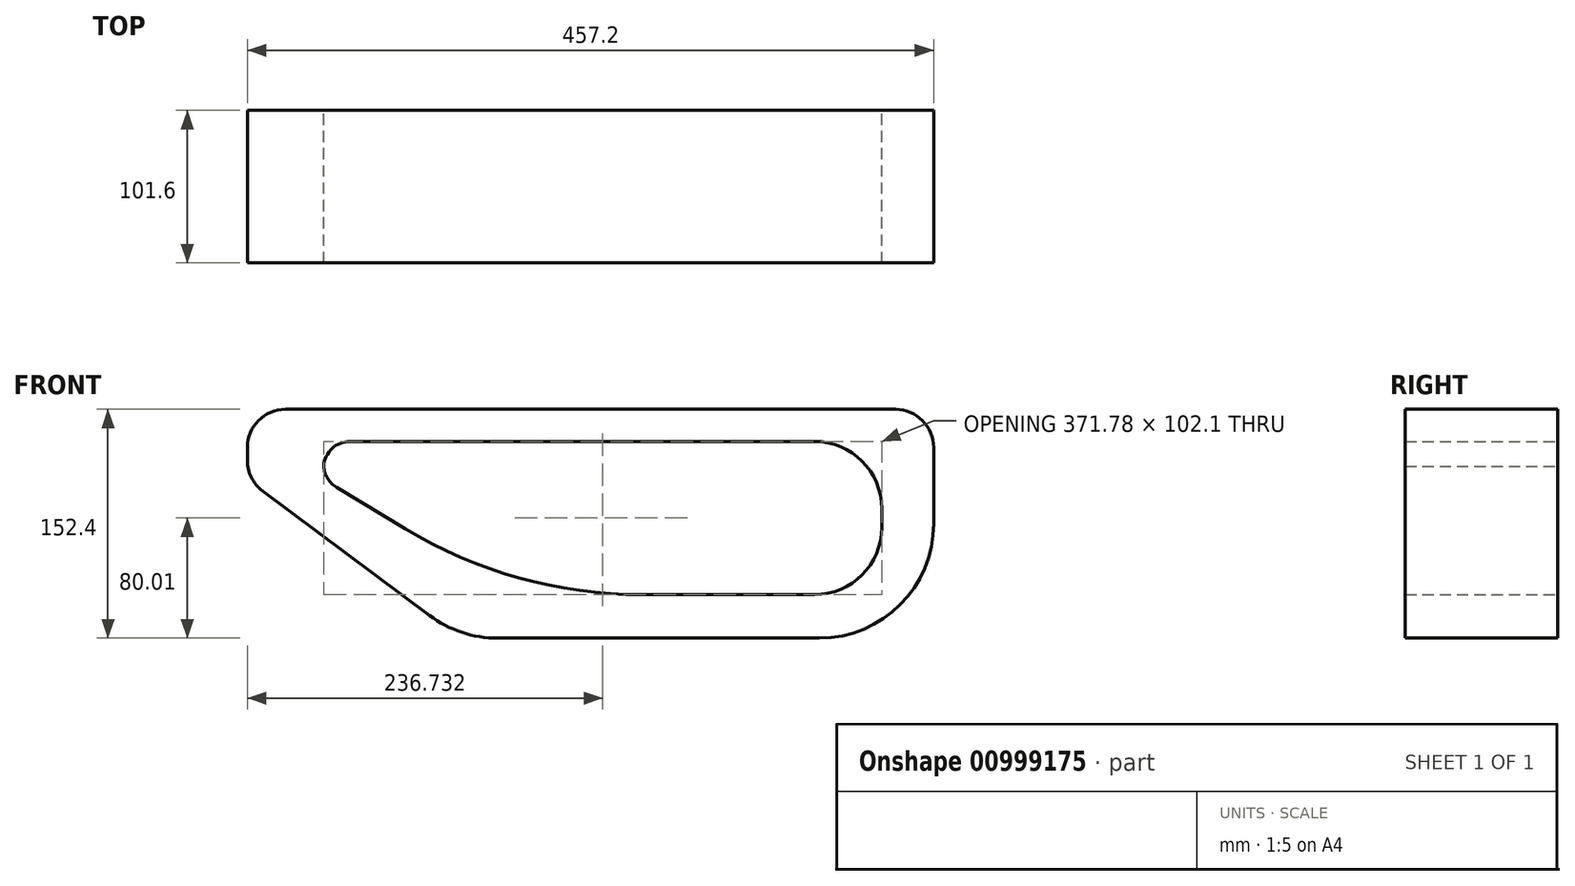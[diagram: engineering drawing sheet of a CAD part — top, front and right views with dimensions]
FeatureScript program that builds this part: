
annotation { "Feature Type Name" : "Feature", "Feature Type Description" : "" }
export const myFeature = defineFeature(function(context is Context, id is Id, definition is map)
    precondition{}
    {
        {
            var Q0;
            Q0=qCreatedBy(makeId("Front.planeOp"),FACE);
            var sketch = newSketch(context, id + "F0", { "sketchPlane" : qUnion([Q0])});
            skLineSegment(sketch, "E0.top", {"start": v(228.6, 76.2) * mm, "end": v(-228.6, 76.2) * mm});
            skLineSegment(sketch, "E0.left", {"start": v(228.6, -76.2) * mm, "end": v(228.6, 76.2) * mm});
            skPoint(sketch, "E0.middle", {"position": v(0, 0) * mm});
            skLineSegment(sketch, "E1", {"start": v(-228.6, 29.46) * mm, "end": v(-86.97, -76.2) * mm});
            skLineSegment(sketch, "E2", {"start": v(-177.8, 29.46) * mm, "end": v(-50.81, -47.24) * mm});
            skLineSegment(sketch, "E3", {"start": v(-50.81, -47.24) * mm, "end": v(194.02, -47.24) * mm});
            skLineSegment(sketch, "E4", {"start": v(-86.97, -76.2) * mm, "end": v(228.6, -76.2) * mm});
            skLineSegment(sketch, "E5", {"start": v(-228.6, 76.2) * mm, "end": v(-228.6, 29.46) * mm});
            skLineSegment(sketch, "E6", {"start": v(-177.8, 29.46) * mm, "end": v(-177.8, 54.86) * mm});
            skLineSegment(sketch, "E7", {"start": v(-177.8, 54.86) * mm, "end": v(194.02, 54.86) * mm});
            skLineSegment(sketch, "E8", {"start": v(194.02, 54.86) * mm, "end": v(194.02, -47.24) * mm});
            skSolve(sketch);
        }
        {
            var Q0;
            Q0=makeQuery(id+"F0.imprint","IMPRINT",FACE,{"disambiguationData":[TD([[makeQuery(id+"F0.imprint","IMPRINT",EDGE,{"derivedFrom":sQuery(id+"F0.wireOp",EDGE,"E0.top")}),1.0]])]});
            extrude(context, id + "F1", {"entities" : qUnion([Q0]), "depth" : 101.6 * mm, "offsetDistance" : 25.4 * mm});
        }
        {
            var Q0;
            Q0=makeQuery(id+"F1.opExtrude","SWEPT_EDGE",EDGE,{"disambiguationData":[OSD([sQuery(id+"F0.wireOp",EDGE,"E0.top"),sQuery(id+"F0.wireOp",EDGE,"E5")])]});
            var Q1;
            Q1=makeQuery(id+"F1.opExtrude","SWEPT_EDGE",EDGE,{"disambiguationData":[OSD([sQuery(id+"F0.wireOp",EDGE,"E1"),sQuery(id+"F0.wireOp",EDGE,"E5")])]});
            fillet(context, id + "F2", {"entities" : qUnion([Q0, Q1]), "radius" : 25.4 * mm, "tangentPropagation" : true, "allowEdgeOverflow" : false});
        }
        {
            var Q0;
            Q0=makeQuery(id+"F1.opExtrude","SWEPT_EDGE",EDGE,{"disambiguationData":[OSD([sQuery(id+"F0.wireOp",EDGE,"E1"),sQuery(id+"F0.wireOp",EDGE,"E4")])]});
            var Q1;
            Q1=makeQuery(id+"F1.opExtrude","SWEPT_EDGE",EDGE,{"disambiguationData":[OSD([sQuery(id+"F0.wireOp",EDGE,"E0.left"),sQuery(id+"F0.wireOp",EDGE,"E4")])]});
            fillet(context, id + "F3", {"entities" : qUnion([Q0, Q1]), "radius" : 76.2 * mm, "tangentPropagation" : true, "allowEdgeOverflow" : false});
        }
        {
            var Q0;
            Q0=makeQuery(id+"F1.opExtrude","SWEPT_EDGE",EDGE,{"disambiguationData":[OSD([sQuery(id+"F0.wireOp",EDGE,"E0.top"),sQuery(id+"F0.wireOp",EDGE,"E0.left")])]});
            fillet(context, id + "F4", {"entities" : qUnion([Q0]), "radius" : 25.4 * mm, "tangentPropagation" : true, "allowEdgeOverflow" : false});
        }
        {
            var Q0;
            Q0=makeQuery(id+"F1.opExtrude","SWEPT_EDGE",EDGE,{"disambiguationData":[OSD([sQuery(id+"F0.wireOp",EDGE,"E2"),sQuery(id+"F0.wireOp",EDGE,"E6")])]});
            var Q1;
            Q1=makeQuery(id+"F1.opExtrude","SWEPT_EDGE",EDGE,{"disambiguationData":[OSD([sQuery(id+"F0.wireOp",EDGE,"E6"),sQuery(id+"F0.wireOp",EDGE,"E7")])]});
            fillet(context, id + "F5", {"entities" : qUnion([Q0, Q1]), "radius" : 17.78 * mm, "tangentPropagation" : true, "allowEdgeOverflow" : false});
        }
        {
            var Q0;
            Q0=makeQuery(id+"F1.opExtrude","SWEPT_EDGE",EDGE,{"disambiguationData":[OSD([sQuery(id+"F0.wireOp",EDGE,"E3"),sQuery(id+"F0.wireOp",EDGE,"E8")])]});
            var Q1;
            Q1=makeQuery(id+"F1.opExtrude","SWEPT_EDGE",EDGE,{"disambiguationData":[OSD([sQuery(id+"F0.wireOp",EDGE,"E7"),sQuery(id+"F0.wireOp",EDGE,"E8")])]});
            fillet(context, id + "F6", {"entities" : qUnion([Q0, Q1]), "radius" : 44.76 * mm, "tangentPropagation" : true, "allowEdgeOverflow" : false});
        }
        {
            var Q0;
            Q0=makeQuery(id+"F1.opExtrude","SWEPT_EDGE",EDGE,{"disambiguationData":[OSD([sQuery(id+"F0.wireOp",EDGE,"E2"),sQuery(id+"F0.wireOp",EDGE,"E3")])]});
            fillet(context, id + "F7", {"entities" : qUnion([Q0]), "radius" : 304.8 * mm, "tangentPropagation" : true, "allowEdgeOverflow" : false});
        }
    });
